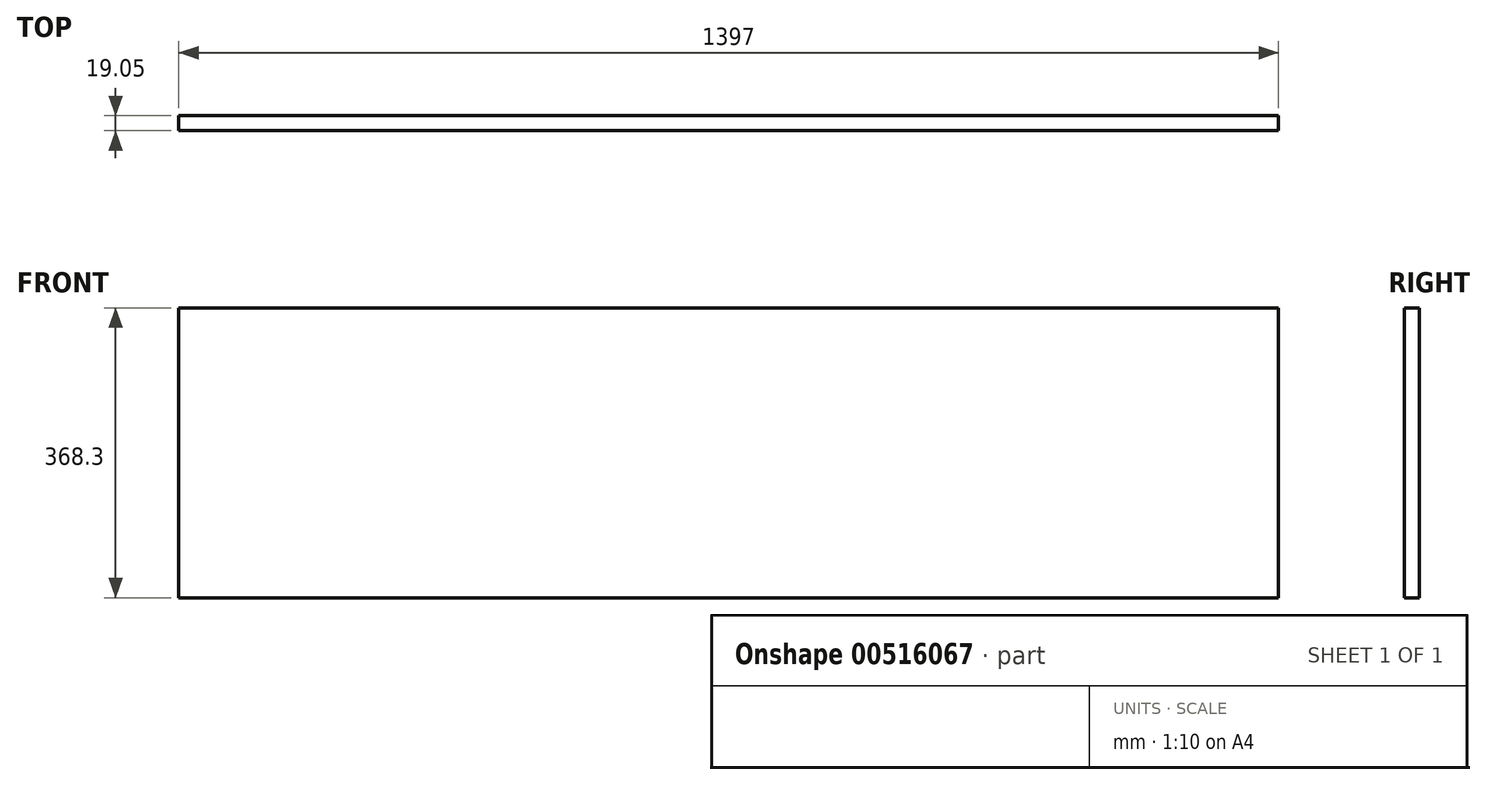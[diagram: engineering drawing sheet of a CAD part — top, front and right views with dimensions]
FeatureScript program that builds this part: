
annotation { "Feature Type Name" : "Feature", "Feature Type Description" : "" }
export const myFeature = defineFeature(function(context is Context, id is Id, definition is map)
    precondition{}
    {
        {
            var Q0;
            Q0=qCreatedBy(makeId("Front.planeOp"),FACE);
            var sketch = newSketch(context, id + "F0", { "sketchPlane" : qUnion([Q0])});
            skLineSegment(sketch, "E0.bottom", {"start": v(698.5, -184.15) * mm, "end": v(-698.5, -184.15) * mm});
            skLineSegment(sketch, "E0.top", {"start": v(698.5, 184.15) * mm, "end": v(-698.5, 184.15) * mm});
            skLineSegment(sketch, "E0.left", {"start": v(698.5, -184.15) * mm, "end": v(698.5, 184.15) * mm});
            skLineSegment(sketch, "E0.right", {"start": v(-698.5, -184.15) * mm, "end": v(-698.5, 184.15) * mm});
            skPoint(sketch, "E0.middle", {"position": v(0, 0) * mm});
            skSolve(sketch);
        }
        {
            var Q0;
            Q0=makeQuery(id+"F0.imprint","IMPRINT",FACE,{"disambiguationData":[TD([[makeQuery(id+"F0.imprint","IMPRINT",EDGE,{"derivedFrom":sQuery(id+"F0.wireOp",EDGE,"E0.bottom")}),-1.0]])]});
            extrude(context, id + "F1", {"entities" : qUnion([Q0]), "depth" : 19.05 * mm, "offsetDistance" : 25.4 * mm});
        }
    });
